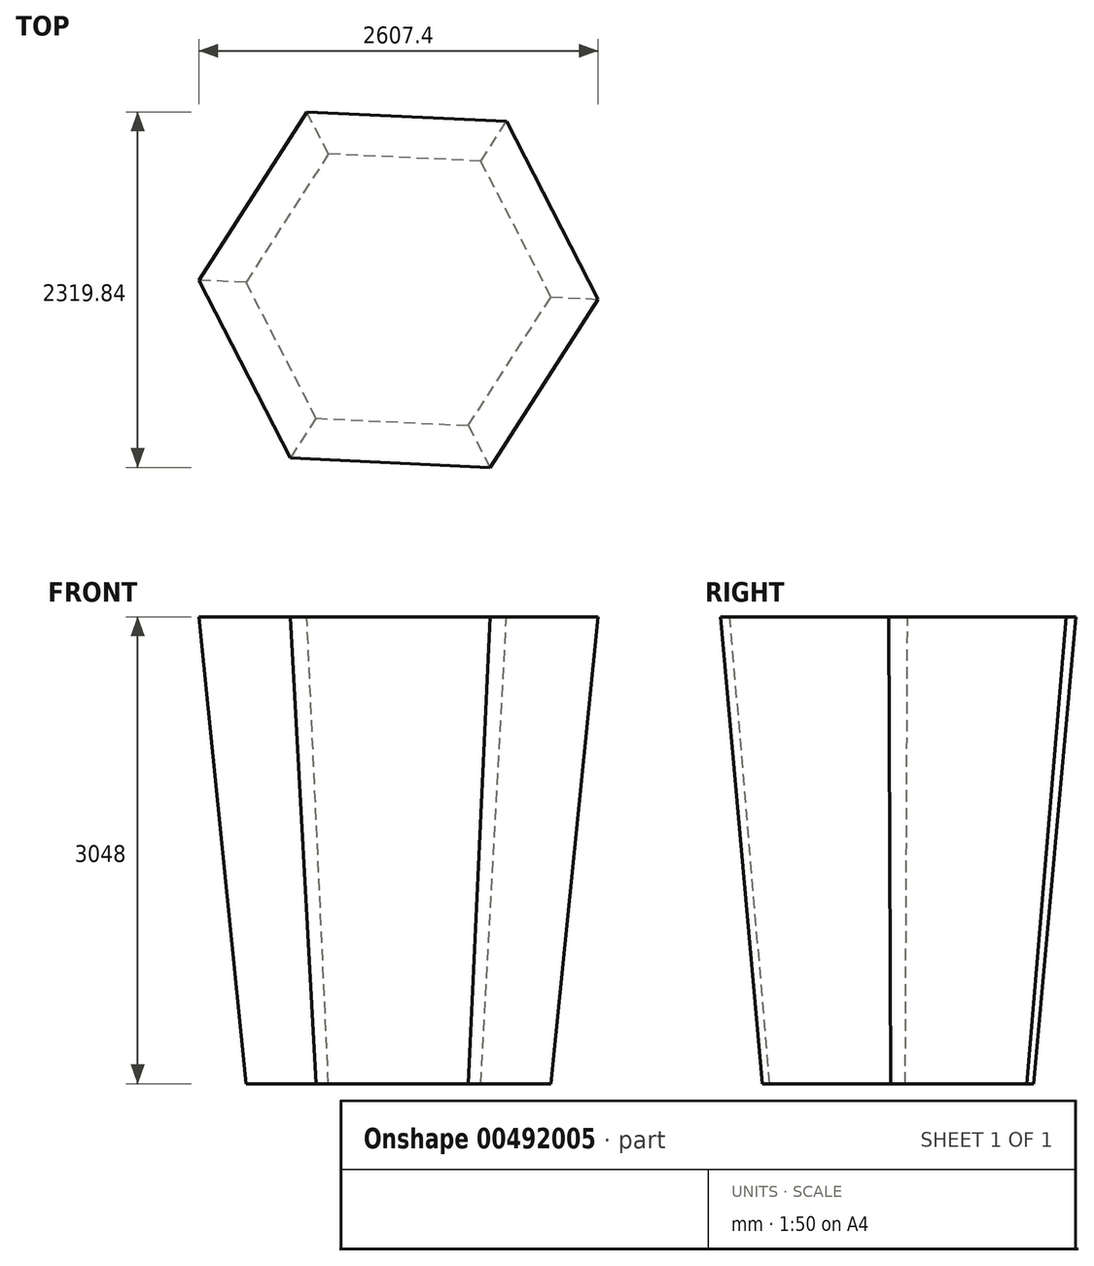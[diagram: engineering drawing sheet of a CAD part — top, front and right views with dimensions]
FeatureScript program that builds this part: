
annotation { "Feature Type Name" : "Feature", "Feature Type Description" : "" }
export const myFeature = defineFeature(function(context is Context, id is Id, definition is map)
    precondition{}
    {
        {
            var Q0;
            Q0=qCreatedBy(makeId("Top.planeOp"),FACE);
            var sketch = newSketch(context, id + "F0", { "sketchPlane" : qUnion([Q0])});
            skCircle(sketch, "E0.cCircle", {"center": v(0, 0) * mm, "radius": 1130.3 * mm, "construction": true});
            skLineSegment(sketch, "E0.0", {"start": v(705.34, 1098.15) * mm, "end": v(1303.7, -61.77) * mm});
            skLineSegment(sketch, "E0.1", {"start": v(1303.7, -61.77) * mm, "end": v(598.35, -1159.92) * mm});
            skLineSegment(sketch, "E0.2", {"start": v(598.35, -1159.92) * mm, "end": v(-705.34, -1098.15) * mm});
            skLineSegment(sketch, "E0.3", {"start": v(-705.34, -1098.15) * mm, "end": v(-1303.7, 61.77) * mm});
            skLineSegment(sketch, "E0.4", {"start": v(-1303.7, 61.77) * mm, "end": v(-598.35, 1159.92) * mm});
            skLineSegment(sketch, "E0.5", {"start": v(-598.35, 1159.92) * mm, "end": v(705.34, 1098.15) * mm});
            skPoint(sketch, "E0.0.midPoint", {"position": v(1004.52, 518.19) * mm});
            skSolve(sketch);
        }
        {
            var Q0;
            Q0=makeQuery(id+"F0.imprint","IMPRINT",FACE,{"disambiguationData":[TD([[makeQuery(id+"F0.imprint","IMPRINT",EDGE,{"derivedFrom":sQuery(id+"F0.wireOp",EDGE,"E0.0")}),-1.0]])]});
            var Q1;
            Q1 = qSketchRegion(id + "F0", true);
            extrude(context, id + "F1", {"entities" : qUnion([Q0, Q1]), "oppositeDirection" : true, "depth" : 3048 * mm, "hasDraft" : true, "draftAngle" : 5 * degree, "draftPullDirection" : true});
        }
    });
